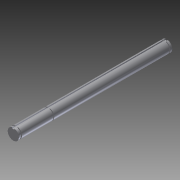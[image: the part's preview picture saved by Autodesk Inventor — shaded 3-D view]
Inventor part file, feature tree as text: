
AUTODESK INVENTOR PART (.ipt)
format: ipt  version: 2012 (Build 160160000, 160)  size: 117,760 bytes
history: native  units: in
note: dims shown in document units (in); Inventor stores cm internally (conversion verified against a paired STEP export)
features: extrude x4, sketch x4, plane x3, projected_geometry x1
ambient origin geometry x8: Origin, YZ Plane, XZ Plane, XY Plane, X Axis, Y Axis, Z Axis, Center Point
bodies: Solid1 (feature_tree)
feature tree (12):
  extrude  "Extrusion1"  Depth=5.125in TaperAngle=0.0deg
  plane  "Work Plane1"
  extrude  "Extrusion2"  Depth=0.0787in
  plane  "Work Plane2"
  extrude  "Extrusion3"  Depth=0.1481in
  plane  "Work Plane3"
  extrude  "Extrusion4"  Depth=0.03in
  sketch  "Sketch1"  dims[d0=0.375in d1=5.125in d2=0.0in]
  sketch  "Sketch2"  dims[d3=0.0787in d4=0.0787in]
  projected_geometry  "Projected Loop1"
  sketch  "Sketch3"  dims[d5=0.0394in d6=0.1481in]
  sketch  "Sketch4"  dims[d7=-0.0625in d9=0.03in d10=0.03in d11=0.0in d13=0.03in d14=0.0in d15=-0.0625in d16=0.04in d17=0.0in d22=-1.15in]
